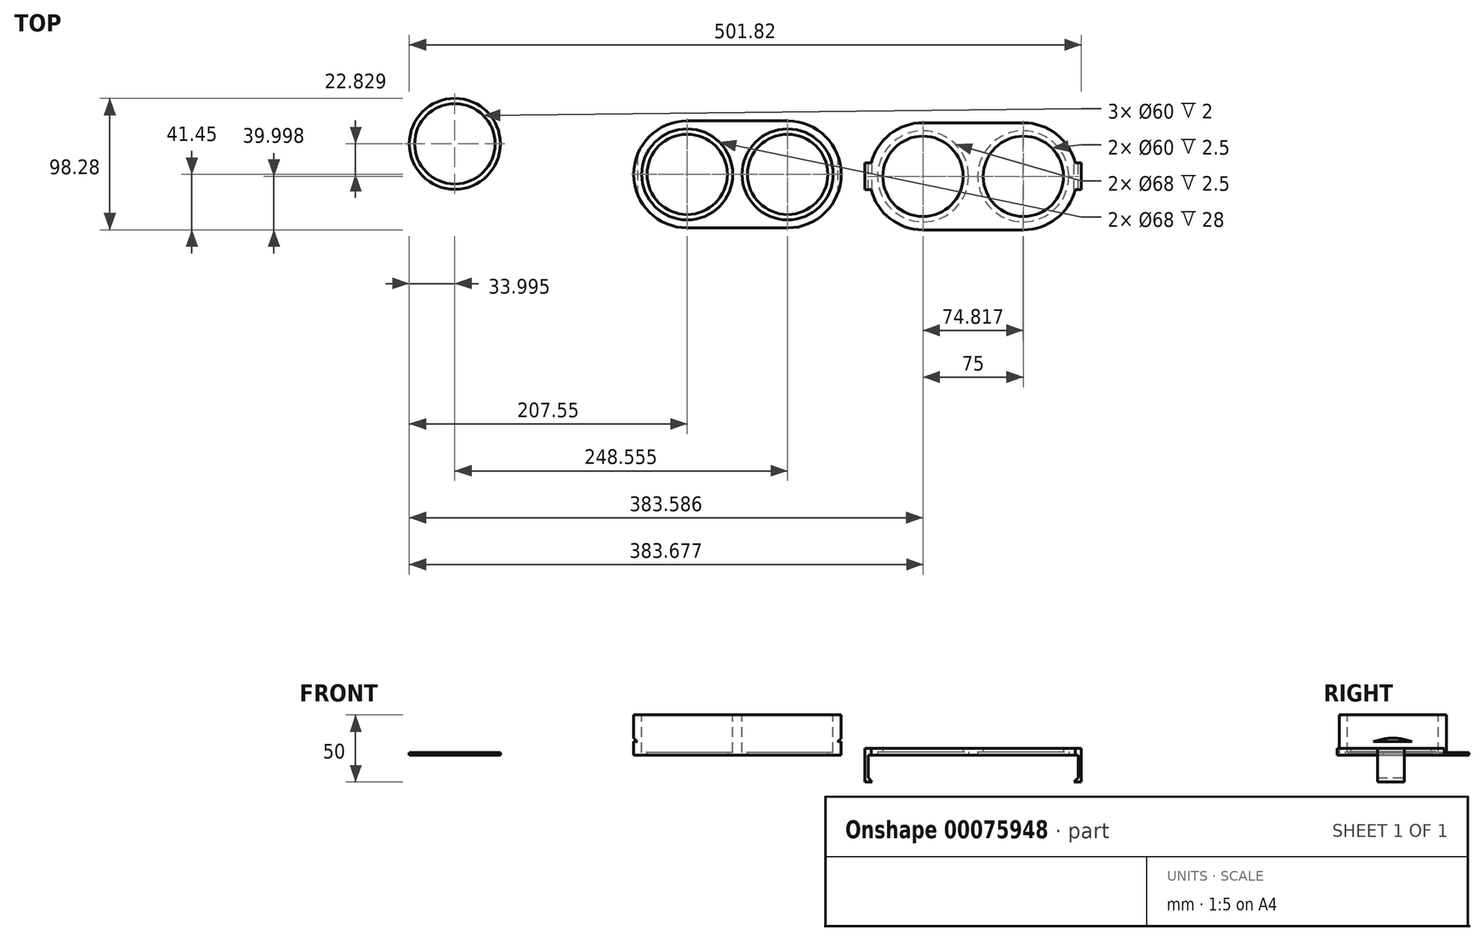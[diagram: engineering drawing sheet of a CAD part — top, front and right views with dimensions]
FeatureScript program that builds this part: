
annotation { "Feature Type Name" : "Feature", "Feature Type Description" : "" }
export const myFeature = defineFeature(function(context is Context, id is Id, definition is map)
    precondition{}
    {
        {
            var Q0;
            Q0=qCreatedBy(makeId("Top.planeOp"),FACE);
            var sketch = newSketch(context, id + "F0", { "sketchPlane" : qUnion([Q0])});
            skLineSegment(sketch, "E0", {"start": v(-37.5, 40) * mm, "end": v(37.5, 40) * mm});
            skLineSegment(sketch, "E1", {"start": v(-37.5, -40) * mm, "end": v(37.5, -40) * mm});
            skArc(sketch, "E2", {"start": v(-37.5, 40) * mm, "mid": v(-77.5, 0) * mm, "end": v(-37.5, -40) * mm});
            skArc(sketch, "E3", {"start": v(37.5, -40) * mm, "mid": v(77.5, 0) * mm, "end": v(37.5, 40) * mm});
            skCircle(sketch, "E4", {"center": v(-37.5, 0) * mm, "radius": 30 * mm});
            skCircle(sketch, "E5", {"center": v(37.5, 0) * mm, "radius": 30 * mm});
            skSolve(sketch);
        }
        {
            var Q0;
            Q0 = qSketchRegion(id + "F0", true);
            extrude(context, id + "F1", {"entities" : qUnion([Q0]), "depth" : 30 * mm});
        }
        {
            var Q0;
            Q0=makeQuery(id+"F1.opExtrude","CAP_FACE",FACE,{"disambiguationData":[OSD([sQuery(id+"F0.wireOp",EDGE,"E0"),sQuery(id+"F0.wireOp",EDGE,"E1"),sQuery(id+"F0.wireOp",EDGE,"E2"),sQuery(id+"F0.wireOp",EDGE,"E3"),sQuery(id+"F0.wireOp",EDGE,"E4"),sQuery(id+"F0.wireOp",EDGE,"E5")])],"isStart":false});
            var sketch = newSketch(context, id + "F2", { "sketchPlane" : qUnion([Q0])});
            skCircle(sketch, "E6", {"center": v(-37.5, 0) * mm, "radius": 34 * mm});
            skCircle(sketch, "E7", {"center": v(37.5, 0) * mm, "radius": 34 * mm});
            skSolve(sketch);
        }
        {
            var Q0;
            Q0 = qSketchRegion(id + "F2", true);
            extrude(context, id + "F3", {"entities" : qUnion([Q0]), "operationType" : NewBodyOperationType.REMOVE, "oppositeDirection" : true, "depth" : 28 * mm});
        }
        {
            var Q0;
            Q0=qCreatedBy(makeId("Top.planeOp"),FACE);
            var sketch = newSketch(context, id + "F4", { "sketchPlane" : qUnion([Q0])});
            skCircle(sketch, "E8", {"center": v(-211.05, 22.83) * mm, "radius": 30 * mm});
            skCircle(sketch, "E9", {"center": v(-211.05, 22.83) * mm, "radius": 34 * mm});
            skSolve(sketch);
        }
        {
            var Q0;
            Q0 = qSketchRegion(id + "F4", true);
            extrude(context, id + "F5", {"entities" : qUnion([Q0]), "depth" : 2 * mm});
        }
        {
            var Q0;
            Q0=qCreatedBy(makeId("Top.planeOp"),FACE);
            var sketch = newSketch(context, id + "F6", { "sketchPlane" : qUnion([Q0])});
            skLineSegment(sketch, "E10", {"start": v(138.54, 38.55) * mm, "end": v(213.54, 38.55) * mm});
            skLineSegment(sketch, "E11", {"start": v(138.54, -41.45) * mm, "end": v(213.54, -41.45) * mm});
            skArc(sketch, "E12", {"start": v(138.54, 38.55) * mm, "mid": v(98.54, -1.45) * mm, "end": v(138.54, -41.45) * mm});
            skArc(sketch, "E13", {"start": v(213.54, -41.45) * mm, "mid": v(253.54, -1.45) * mm, "end": v(213.54, 38.55) * mm});
            skCircle(sketch, "E14", {"center": v(138.54, -1.45) * mm, "radius": 30 * mm});
            skCircle(sketch, "E15", {"center": v(213.54, -1.45) * mm, "radius": 30 * mm});
            skLineSegment(sketch, "E16", {"start": v(176.04, -41.45) * mm, "end": v(176.04, 38.55) * mm, "construction": true});
            skSolve(sketch);
        }
        {
            var Q0;
            Q0 = qSketchRegion(id + "F6", true);
            extrude(context, id + "F7", {"entities" : qUnion([Q0]), "depth" : 5 * mm});
        }
        {
            var Q0;
            Q0=makeQuery(id+"F7.opExtrude","CAP_FACE",FACE,{"disambiguationData":[OSD([sQuery(id+"F6.wireOp",EDGE,"E10"),sQuery(id+"F6.wireOp",EDGE,"E11"),sQuery(id+"F6.wireOp",EDGE,"E12"),sQuery(id+"F6.wireOp",EDGE,"E13"),sQuery(id+"F6.wireOp",EDGE,"E14"),sQuery(id+"F6.wireOp",EDGE,"E15")])],"isStart":true});
            var sketch = newSketch(context, id + "F8", { "sketchPlane" : qUnion([Q0])});
            skCircle(sketch, "E17", {"center": v(138.63, 1.45) * mm, "radius": 34 * mm});
            skCircle(sketch, "E18", {"center": v(213.44, 1.45) * mm, "radius": 34 * mm});
            skSolve(sketch);
        }
        {
            var Q0;
            Q0 = qSketchRegion(id + "F8", true);
            extrude(context, id + "F9", {"entities" : qUnion([Q0]), "operationType" : NewBodyOperationType.REMOVE, "oppositeDirection" : true, "depth" : 2.5 * mm});
        }
        {
            var Q0;
            Q0=makeQuery(id+"F7.opExtrude","CAP_FACE",FACE,{"disambiguationData":[OSD([sQuery(id+"F6.wireOp",EDGE,"E10"),sQuery(id+"F6.wireOp",EDGE,"E11"),sQuery(id+"F6.wireOp",EDGE,"E12"),sQuery(id+"F6.wireOp",EDGE,"E13"),sQuery(id+"F6.wireOp",EDGE,"E14"),sQuery(id+"F6.wireOp",EDGE,"E15")])],"isStart":true});
            var sketch = newSketch(context, id + "F10", { "sketchPlane" : qUnion([Q0])});
            skLineSegment(sketch, "E19.bottom", {"start": v(95.3, 11.45) * mm, "end": v(99.8, 11.45) * mm});
            skLineSegment(sketch, "E19.top", {"start": v(95.3, -8.55) * mm, "end": v(99.8, -8.55) * mm});
            skLineSegment(sketch, "E19.left", {"start": v(95.3, 11.45) * mm, "end": v(95.3, -8.55) * mm});
            skLineSegment(sketch, "E19.right", {"start": v(99.8, 11.45) * mm, "end": v(99.8, -8.55) * mm});
            skLineSegment(sketch, "E20.bottom", {"start": v(252.27, 11.45) * mm, "end": v(256.77, 11.45) * mm});
            skLineSegment(sketch, "E20.top", {"start": v(252.27, -8.55) * mm, "end": v(256.77, -8.55) * mm});
            skLineSegment(sketch, "E20.left", {"start": v(252.27, 11.45) * mm, "end": v(252.27, -8.55) * mm});
            skLineSegment(sketch, "E20.right", {"start": v(256.77, 11.45) * mm, "end": v(256.77, -8.55) * mm});
            skLineSegment(sketch, "E21", {"start": v(87.76, 1.45) * mm, "end": v(264.31, 1.45) * mm, "construction": true});
            skLineSegment(sketch, "E22", {"start": v(176.04, 41.45) * mm, "end": v(176.04, -38.55) * mm, "construction": true});
            skPoint(sketch, "E23", {"position": v(176.04, 1.45) * mm});
            skPoint(sketch, "E24", {"position": v(256.77, 1.45) * mm});
            skSolve(sketch);
        }
        {
            var Q0;
            Q0 = qSketchRegion(id + "F10", true);
            var Q1;
            Q1=makeQuery(id+"F7.opExtrude","CAP_FACE",FACE,{"disambiguationData":[OSD([sQuery(id+"F6.wireOp",EDGE,"E10"),sQuery(id+"F6.wireOp",EDGE,"E11"),sQuery(id+"F6.wireOp",EDGE,"E12"),sQuery(id+"F6.wireOp",EDGE,"E13"),sQuery(id+"F6.wireOp",EDGE,"E14"),sQuery(id+"F6.wireOp",EDGE,"E15")])],"isStart":false});
            extrude(context, id + "F11", {"entities" : qUnion([Q0]), "operationType" : NewBodyOperationType.ADD, "endBound" : BoundingType.UP_TO_SURFACE, "oppositeDirection" : true, "endBoundEntityFace" : qUnion([Q1]), "depth" : 25 * mm});
        }
        {
            var Q0;
            Q0=makeQuery(id+"F11.boolean.opBoolean","MERGE",FACE,{"derivedFrom":[makeQuery(id+"F7.opExtrude","CAP_FACE",FACE,{"disambiguationData":[OSD([sQuery(id+"F6.wireOp",EDGE,"E10"),sQuery(id+"F6.wireOp",EDGE,"E11"),sQuery(id+"F6.wireOp",EDGE,"E12"),sQuery(id+"F6.wireOp",EDGE,"E13"),sQuery(id+"F6.wireOp",EDGE,"E14"),sQuery(id+"F6.wireOp",EDGE,"E15")])],"isStart":true}),makeQuery(id+"F11.opExtrude","CAP_FACE",FACE,{"disambiguationData":[OSD([sQuery(id+"F10.wireOp",EDGE,"E19.bottom"),sQuery(id+"F10.wireOp",EDGE,"E19.top"),sQuery(id+"F10.wireOp",EDGE,"E19.left"),sQuery(id+"F10.wireOp",EDGE,"E19.right")])],"isStart":true}),makeQuery(id+"F11.opExtrude","CAP_FACE",FACE,{"disambiguationData":[OSD([sQuery(id+"F10.wireOp",EDGE,"E20.bottom"),sQuery(id+"F10.wireOp",EDGE,"E20.top"),sQuery(id+"F10.wireOp",EDGE,"E20.left"),sQuery(id+"F10.wireOp",EDGE,"E20.right")])],"isStart":true})]});
            var sketch = newSketch(context, id + "F12", { "sketchPlane" : qUnion([Q0])});
            skLineSegment(sketch, "E25.bottom", {"start": v(95.3, 11.45) * mm, "end": v(97.56, 11.45) * mm});
            skLineSegment(sketch, "E25.top", {"start": v(95.3, -8.55) * mm, "end": v(97.56, -8.55) * mm});
            skLineSegment(sketch, "E25.left", {"start": v(95.3, 11.45) * mm, "end": v(95.3, -8.55) * mm});
            skLineSegment(sketch, "E25.right", {"start": v(97.56, 11.45) * mm, "end": v(97.56, -8.55) * mm});
            skLineSegment(sketch, "E26.bottom", {"start": v(256.77, 11.45) * mm, "end": v(254.52, 11.45) * mm});
            skLineSegment(sketch, "E26.top", {"start": v(256.77, -8.55) * mm, "end": v(254.52, -8.55) * mm});
            skLineSegment(sketch, "E26.left", {"start": v(256.77, 11.45) * mm, "end": v(256.77, -8.55) * mm});
            skLineSegment(sketch, "E26.right", {"start": v(254.52, 11.45) * mm, "end": v(254.52, -8.55) * mm});
            skSolve(sketch);
        }
        {
            var Q0;
            Q0 = qSketchRegion(id + "F12", true);
            extrude(context, id + "F13", {"entities" : qUnion([Q0]), "operationType" : NewBodyOperationType.ADD, "depth" : 20 * mm});
        }
        {
            var Q0;
            Q0=makeQuery(id+"F13.boolean.opBoolean","MERGE",FACE,{"derivedFrom":[makeQuery(id+"F11.opExtrude","SWEPT_FACE",FACE,{"disambiguationData":[OSD([sQuery(id+"F10.wireOp",EDGE,"E19.top")])]}),makeQuery(id+"F13.opExtrude","SWEPT_FACE",FACE,{"disambiguationData":[OSD([sQuery(id+"F12.wireOp",EDGE,"E25.top")])]})]});
            var sketch = newSketch(context, id + "F14", { "sketchPlane" : qUnion([Q0])});
            skLineSegment(sketch, "E27", {"start": v(-97.56, -17) * mm, "end": v(-100.56, -20) * mm});
            skLineSegment(sketch, "E28", {"start": v(-100.56, -20) * mm, "end": v(-97.56, -20) * mm});
            skLineSegment(sketch, "E29", {"start": v(-97.56, -20) * mm, "end": v(-97.56, -17) * mm});
            skLineSegment(sketch, "E30", {"start": v(-254.52, -17) * mm, "end": v(-251.52, -20) * mm});
            skLineSegment(sketch, "E31", {"start": v(-251.52, -20) * mm, "end": v(-254.52, -20) * mm});
            skLineSegment(sketch, "E32", {"start": v(-254.52, -20) * mm, "end": v(-254.52, -17) * mm});
            skSolve(sketch);
        }
        {
            var Q0;
            Q0 = qSketchRegion(id + "F14", true);
            var Q1;
            Q1=makeQuery(id+"F13.boolean.opBoolean","MERGE",FACE,{"derivedFrom":[makeQuery(id+"F11.opExtrude","SWEPT_FACE",FACE,{"disambiguationData":[OSD([sQuery(id+"F10.wireOp",EDGE,"E20.bottom")])]}),makeQuery(id+"F13.opExtrude","SWEPT_FACE",FACE,{"disambiguationData":[OSD([sQuery(id+"F12.wireOp",EDGE,"E26.bottom")])]})]});
            extrude(context, id + "F15", {"entities" : qUnion([Q0]), "operationType" : NewBodyOperationType.ADD, "endBound" : BoundingType.UP_TO_SURFACE, "oppositeDirection" : true, "endBoundEntityFace" : qUnion([Q1]), "depth" : 25 * mm});
        }
        {
            var Q0;
            Q0=makeQuery(id+"F1.opExtrude","SWEPT_FACE",FACE,{"disambiguationData":[OSD([sQuery(id+"F0.wireOp",EDGE,"E1")])]});
            var sketch = newSketch(context, id + "F16", { "sketchPlane" : qUnion([Q0])});
            skLineSegment(sketch, "E33", {"start": v(-77.8, 13) * mm, "end": v(-77.8, 10) * mm});
            skLineSegment(sketch, "E34", {"start": v(-77.8, 10) * mm, "end": v(-74.8, 10) * mm});
            skLineSegment(sketch, "E35", {"start": v(-74.8, 10) * mm, "end": v(-77.8, 13) * mm});
            skLineSegment(sketch, "E36.MirrorCS", {"start": v(74.8, 10) * mm, "end": v(77.8, 13) * mm});
            skLineSegment(sketch, "E37.MirrorCS", {"start": v(77.8, 10) * mm, "end": v(74.8, 10) * mm});
            skLineSegment(sketch, "E38.MirrorCS", {"start": v(77.8, 13) * mm, "end": v(77.8, 10) * mm});
            skSolve(sketch);
        }
        {
            var Q0;
            Q0 = qSketchRegion(id + "F16", true);
            extrude(context, id + "F17", {"entities" : qUnion([Q0]), "operationType" : NewBodyOperationType.REMOVE, "endBound" : BoundingType.THROUGH_ALL, "oppositeDirection" : true, "depth" : 25 * mm});
        }
    });
